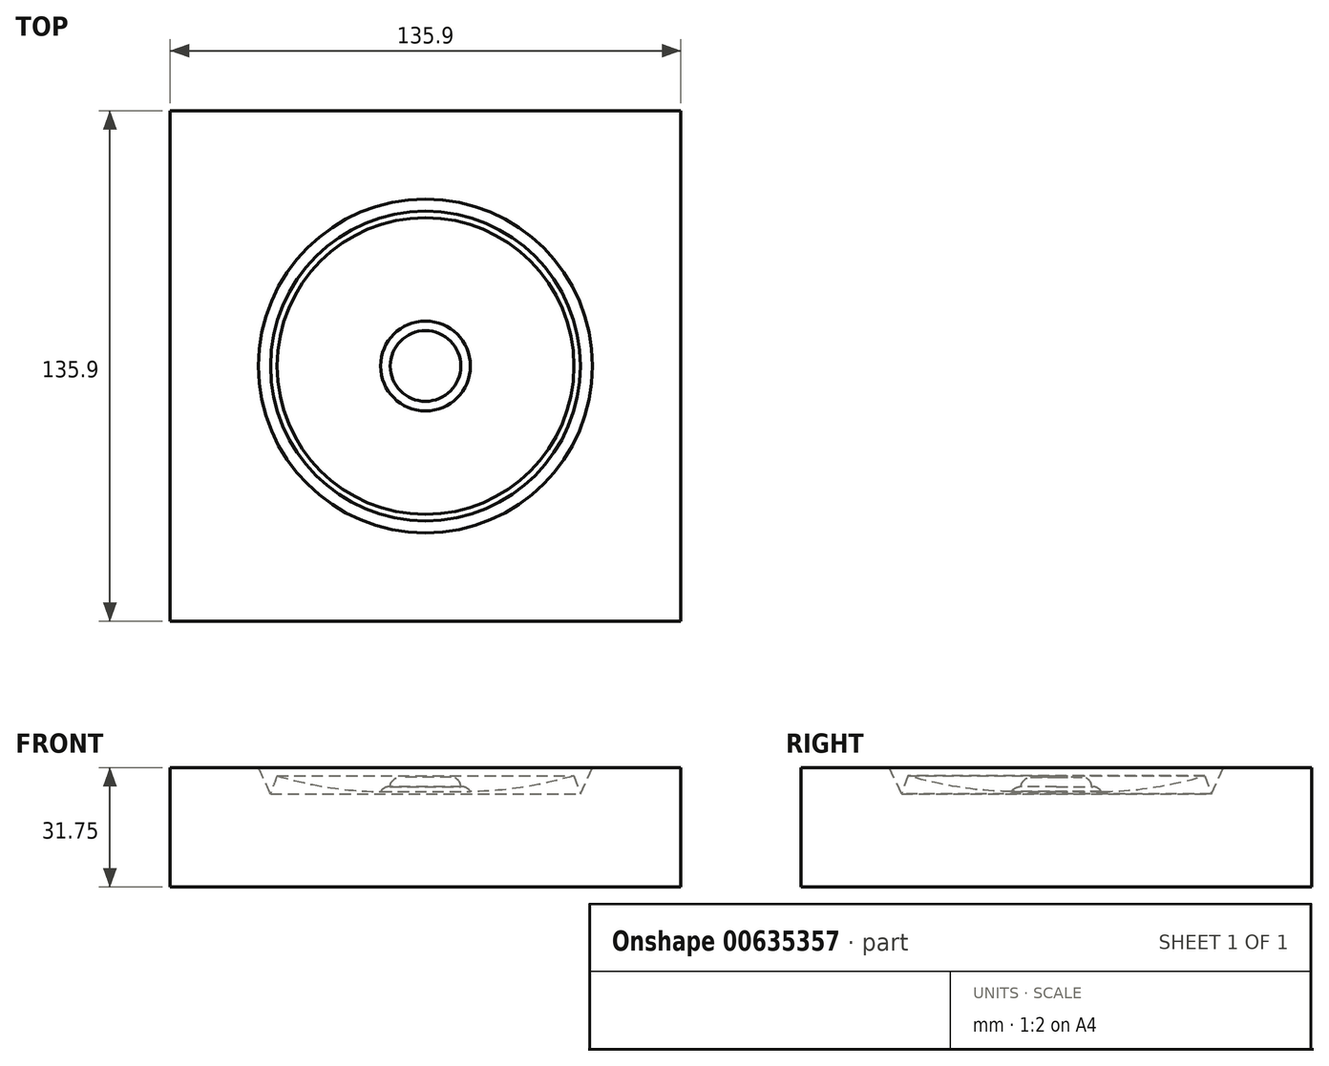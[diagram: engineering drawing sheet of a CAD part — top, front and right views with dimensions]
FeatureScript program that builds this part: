
annotation { "Feature Type Name" : "Feature", "Feature Type Description" : "" }
export const myFeature = defineFeature(function(context is Context, id is Id, definition is map)
    precondition{}
    {
        {
            var Q0;
            Q0=qCreatedBy(makeId("Top.planeOp"),FACE);
            var sketch = newSketch(context, id + "F0", { "sketchPlane" : qUnion([Q0])});
            skLineSegment(sketch, "E0.bottom", {"start": v(67.94, -67.94) * mm, "end": v(-67.95, -67.95) * mm});
            skLineSegment(sketch, "E0.top", {"start": v(67.95, 67.95) * mm, "end": v(-67.94, 67.95) * mm});
            skLineSegment(sketch, "E0.left", {"start": v(67.95, -67.94) * mm, "end": v(67.95, 67.95) * mm});
            skLineSegment(sketch, "E0.right", {"start": v(-67.95, -67.95) * mm, "end": v(-67.95, 67.94) * mm});
            skPoint(sketch, "E0.middle", {"position": v(0, 0) * mm});
            skSolve(sketch);
        }
        {
            var Q0;
            Q0 = qSketchRegion(id + "F0", true);
            extrude(context, id + "F1", {"entities" : qUnion([Q0]), "depth" : 31.75 * mm, "offsetDistance" : 25.4 * mm});
        }
        {
            var Q0;
            Q0=qCreatedBy(makeId("Front.planeOp"),FACE);
            var sketch = newSketch(context, id + "F2", { "sketchPlane" : qUnion([Q0])});
            skLineSegment(sketch, "E1", {"start": v(0, 31.75) * mm, "end": v(-44.45, 31.75) * mm});
            skLineSegment(sketch, "E2", {"start": v(-44.45, 31.75) * mm, "end": v(-41.23, 24.84) * mm});
            skLineSegment(sketch, "E3", {"start": v(-41.23, 24.84) * mm, "end": v(-39.5, 29.62) * mm});
            skLineSegment(sketch, "E4", {"start": v(-39.5, 29.62) * mm, "end": v(-11.95, 25.4) * mm, "construction": true});
            skLineSegment(sketch, "E5", {"start": v(-11.95, 25.4) * mm, "end": v(-11.95, 26.67) * mm});
            skLineSegment(sketch, "E6", {"start": v(-11.95, 26.67) * mm, "end": v(-9.4, 26.67) * mm});
            skLineSegment(sketch, "E7", {"start": v(-9.4, 26.67) * mm, "end": v(-9.4, 29.21) * mm});
            skLineSegment(sketch, "E8", {"start": v(-9.4, 29.21) * mm, "end": v(0, 29.21) * mm});
            skLineSegment(sketch, "E9", {"start": v(0, 29.21) * mm, "end": v(0, 31.75) * mm});
            skLineSegment(sketch, "E10", {"start": v(0, 23.32) * mm, "end": v(0, 19.89) * mm, "construction": true});
            skArc(sketch, "E11", {"start": v(-39.5, 29.62) * mm, "mid": v(-25.87, 26.54) * mm, "end": v(-11.95, 25.4) * mm});
            skSolve(sketch);
        }
        {
            var Q0;
            Q0 = qSketchRegion(id + "F2", true);
            var Q1;
            Q1=sQuery(id+"F2.wireOp",EDGE,"E10");
            revolve(context, id + "F3", {"operationType" : NewBodyOperationType.REMOVE, "entities" : qUnion([Q0]), "axis" : qUnion([Q1]), "revolveType" : RevolveType.FULL, "oppositeDirection" : true});
        }
        {
            var Q0;
            Q0=makeQuery(id+"F3.boolean.opBoolean","COPY",EDGE,{"derivedFrom":makeQuery(id+"F3.opRevolve","SWEPT_EDGE",EDGE,{"disambiguationData":[OSD([sQuery(id+"F2.wireOp",EDGE,"E7"),sQuery(id+"F2.wireOp",EDGE,"E8")])]})});
            var Q1;
            Q1=makeQuery(id+"F3.boolean.opBoolean","COPY",EDGE,{"derivedFrom":makeQuery(id+"F3.opRevolve","SWEPT_EDGE",EDGE,{"disambiguationData":[OSD([sQuery(id+"F2.wireOp",EDGE,"E5"),sQuery(id+"F2.wireOp",EDGE,"E6")])]})});
            fillet(context, id + "F4", {"entities" : qUnion([Q0, Q1]), "radius" : 2.54 * mm, "tangentPropagation" : true, "allowEdgeOverflow" : false});
        }
    });
